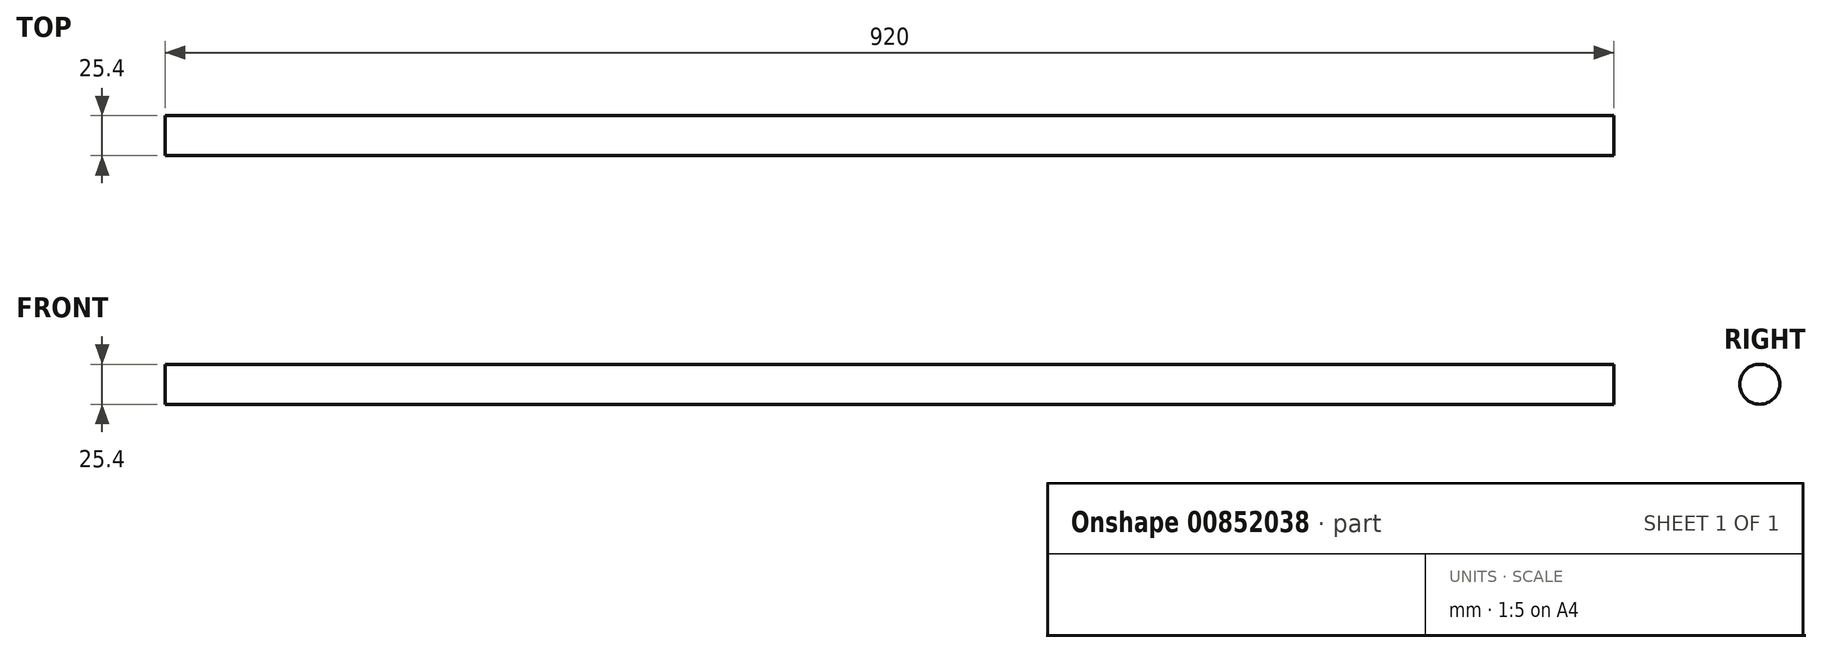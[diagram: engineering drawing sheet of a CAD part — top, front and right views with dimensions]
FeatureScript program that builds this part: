
annotation { "Feature Type Name" : "Feature", "Feature Type Description" : "" }
export const myFeature = defineFeature(function(context is Context, id is Id, definition is map)
    precondition{}
    {
        {
            var Q0;
            Q0=qCreatedBy(makeId("Right.planeOp"),FACE);
            var sketch = newSketch(context, id + "F0", { "sketchPlane" : qUnion([Q0])});
            skCircle(sketch, "E0", {"center": v(0, 0) * mm, "radius": 12.7 * mm});
            skSolve(sketch);
        }
        {
            var Q0;
            Q0=sQuery(id+"F0.wireOp",EDGE,"E0");
            extrude(context, id + "F1", {"bodyType" : ToolBodyType.SURFACE, "surfaceEntities" : qUnion([Q0]), "depth" : 920 * mm, "offsetDistance" : 25.4 * mm});
        }
    });
